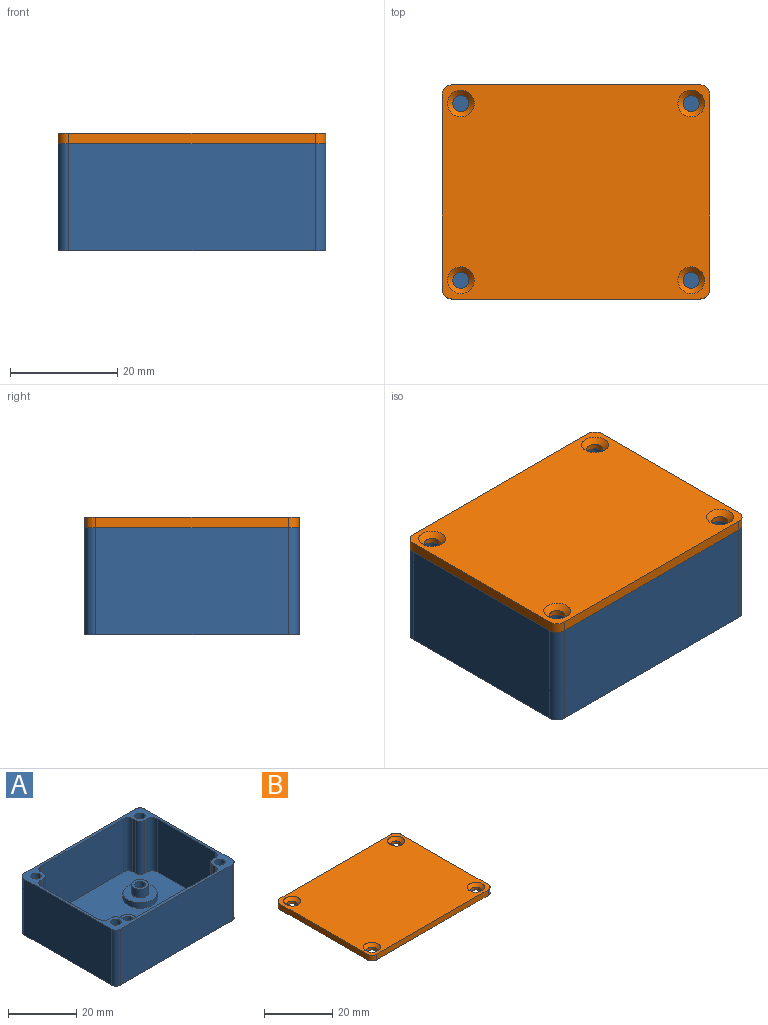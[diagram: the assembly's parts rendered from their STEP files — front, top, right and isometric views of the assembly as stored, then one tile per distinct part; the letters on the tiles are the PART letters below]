
ASSEMBLY  parts=2 mates=1
PART A: 67 faces, bbox 50x40x20 mm
  f0: cylinder r=1.5mm len=4mm, axis (0,0,-1), area 37.7mm2, adj f30,f50
  f1: cylinder r=1.5mm len=4mm, axis (0,0,-1), area 37.7mm2, adj f32,f43
  f2: plane 48x38mm, normal (0,0,1), area 1563.5mm2, adj f3,f4,f5,f6,f13,f14,f15,f16
  f3: plane 24x19mm, normal (-1,0,0), area 456mm2, adj f2,f7,f56,f57
  f4: plane 24x19mm, normal (1,0,0), area 456mm2, adj f2,f7,f53,f62
  f5: plane 34x19mm, normal (0,1,0), area 646mm2, adj f2,f7,f52,f54
  f6: plane 34x19mm, normal (0,-1,0), area 646mm2, adj f2,f7,f58,f60
  f7: plane 50x40mm, normal (0,0,1), area 247.7mm2, adj f3,f4,f5,f6,f8,f9,f10,f11
  f8: plane 46x20mm, normal (0,1,0), area 920mm2, adj f7,f12,f63,f66
  f9: plane 36x20mm, normal (-1,0,0), area 720mm2, adj f7,f12,f63,f64
  f10: plane 46x20mm, normal (0,-1,0), area 920mm2, adj f7,f12,f64,f65
  f11: plane 36x20mm, normal (1,0,0), area 720mm2, adj f7,f12,f65,f66
  f12: plane 50x40mm, normal (0,0,-1), area 1949.8mm2, adj f8,f9,f10,f11,f37,f38,f39,f40
  f13: plane 19x1mm, normal (0,-1,0), area 19mm2, adj f2,f7,f61,f62
  f14: plane 19x1mm, normal (1,0,0), area 19mm2, adj f2,f7,f60,f61
  f15: plane 19x1mm, normal (0,-1,0), area 19mm2, adj f2,f7,f57,f59
  f16: plane 19x1mm, normal (-1,0,0), area 19mm2, adj f2,f7,f58,f59
  f17: plane 19x1mm, normal (0,1,0), area 19mm2, adj f2,f7,f51,f53
  f18: plane 19x1mm, normal (1,0,0), area 19mm2, adj f2,f7,f51,f52
  f19: plane 19x1mm, normal (0,1,0), area 19mm2, adj f2,f7,f55,f56
  f20: plane 19x1mm, normal (-1,0,0), area 19mm2, adj f2,f7,f54,f55
  f21: cylinder r=1.5mm len=10mm, axis (0,0,1), area 94.2mm2, adj f7,f22
  f22: plane 3x3mm, normal (0,0,1), area 7.1mm2, adj f21
  f23: cylinder r=1.5mm len=10mm, axis (0,0,1), area 94.2mm2, adj f7,f24
  f24: plane 3x3mm, normal (0,0,1), area 7.1mm2, adj f23
  f25: cylinder r=1.5mm len=10mm, axis (0,0,1), area 94.2mm2, adj f7,f26
  f26: plane 3x3mm, normal (0,0,1), area 7.1mm2, adj f25
  f27: cylinder r=1.5mm len=10mm, axis (0,0,1), area 94.2mm2, adj f7,f28
  f28: plane 3x3mm, normal (0,0,1), area 7.1mm2, adj f27
  f29: cylinder r=2.5mm len=5mm, axis (0,0,-1), area 47.1mm2, adj f30,f36
  f30: plane 5x5mm, normal (0,0,1), area 12.6mm2, adj f0,f29
  f31: cylinder r=2.5mm len=5mm, axis (0,0,-1), area 47.1mm2, adj f32,f34
  f32: plane 5x5mm, normal (0,0,1), area 12.6mm2, adj f1,f31
  f33: cylinder r=5mm len=10mm, axis (0,0,-1), area 62.8mm2, adj f2,f34
  f34: plane 10x10mm, normal (0,0,1), area 58.9mm2, adj f31,f33
  f35: cylinder r=5mm len=10mm, axis (0,0,-1), area 62.8mm2, adj f2,f36
  f36: plane 10x10mm, normal (0,0,1), area 58.9mm2, adj f29,f35
  f37: plane 3x2mm, normal (1,0,0), area 6mm2, adj f12,f38,f42,f43
  f38: plane 2.6x2mm, normal (0.5,-0.87,0), area 6mm2, adj f12,f37,f39,f43
  f39: plane 2.6x2mm, normal (-0.5,-0.87,0), area 6mm2, adj f12,f38,f40,f43
  f40: plane 3x2mm, normal (-1,0,0), area 6mm2, adj f12,f39,f41,f43
  f41: plane 2.6x2mm, normal (-0.5,0.87,0), area 6mm2, adj f12,f40,f42,f43
  f42: plane 2.6x2mm, normal (0.5,0.87,0), area 6mm2, adj f12,f37,f41,f43
  f43: plane 6x5.2mm, normal (0,0,-1), area 16.3mm2, adj f1,f37,f38,f39,f40,f41,f42
  f44: plane 3x2mm, normal (1,0,0), area 6mm2, adj f12,f45,f49,f50
  f45: plane 2.6x2mm, normal (0.5,-0.87,0), area 6mm2, adj f12,f44,f46,f50
  f46: plane 2.6x2mm, normal (-0.5,-0.87,0), area 6mm2, adj f12,f45,f47,f50
  f47: plane 3x2mm, normal (-1,0,0), area 6mm2, adj f12,f46,f48,f50
  f48: plane 2.6x2mm, normal (-0.5,0.87,0), area 6mm2, adj f12,f47,f49,f50
  f49: plane 2.6x2mm, normal (0.5,0.87,0), area 6mm2, adj f12,f44,f48,f50
  f50: plane 6x5.2mm, normal (0,0,-1), area 16.3mm2, adj f0,f44,f45,f46,f47,f48,f49
  f51: cylinder r=2mm len=19mm, axis (0,0,1), area 59.7mm2, adj f2,f7,f17,f18
  f52: cylinder r=2mm len=19mm, axis (0,0,1), area 59.7mm2, adj f2,f5,f7,f18
  f53: cylinder r=2mm len=19mm, axis (0,0,1), area 59.7mm2, adj f2,f4,f7,f17
  f54: cylinder r=2mm len=19mm, axis (0,0,-1), area 59.7mm2, adj f2,f5,f7,f20
  f55: cylinder r=2mm len=19mm, axis (0,0,1), area 59.7mm2, adj f2,f7,f19,f20
  f56: cylinder r=2mm len=19mm, axis (0,0,1), area 59.7mm2, adj f2,f3,f7,f19
  f57: cylinder r=2mm len=19mm, axis (0,0,-1), area 59.7mm2, adj f2,f3,f7,f15
  f58: cylinder r=2mm len=19mm, axis (0,0,-1), area 59.7mm2, adj f2,f6,f7,f16
  f59: cylinder r=2mm len=19mm, axis (0,0,1), area 59.7mm2, adj f2,f7,f15,f16
  f60: cylinder r=2mm len=19mm, axis (0,0,1), area 59.7mm2, adj f2,f6,f7,f14
  f61: cylinder r=2mm len=19mm, axis (0,0,1), area 59.7mm2, adj f2,f7,f13,f14
  f62: cylinder r=2mm len=19mm, axis (0,0,-1), area 59.7mm2, adj f2,f4,f7,f13
  f63: cylinder r=2mm len=20mm, axis (0,0,1), area 62.8mm2, adj f7,f8,f9,f12
  f64: cylinder r=2mm len=20mm, axis (0,0,-1), area 62.8mm2, adj f7,f9,f10,f12
  f65: cylinder r=2mm len=20mm, axis (0,0,1), area 62.8mm2, adj f7,f10,f11,f12
  f66: cylinder r=2mm len=20mm, axis (0,0,-1), area 62.8mm2, adj f7,f8,f11,f12
PART B: 18 faces, bbox 50x40x2 mm
  f0: plane 46x2mm, normal (0,1,0), area 92mm2, adj f4,f5,f14,f17
  f1: plane 36x2mm, normal (-1,0,0), area 72mm2, adj f4,f5,f14,f15
  f2: plane 46x2mm, normal (0,-1,0), area 92mm2, adj f4,f5,f15,f16
  f3: plane 36x2mm, normal (1,0,0), area 72mm2, adj f4,f5,f16,f17
  f4: plane 50x40mm, normal (0,0,1), area 1918mm2, adj f0,f1,f2,f3,f10,f11,f12,f13
  f5: plane 50x40mm, normal (0,0,-1), area 1968.3mm2, adj f0,f1,f2,f3,f6,f7,f8,f9
  f6: cylinder r=1.5mm len=3mm, axis (0,0,1), area 9.4mm2, adj f5,f13
  f7: cylinder r=1.5mm len=3mm, axis (0,0,1), area 9.4mm2, adj f5,f12
  f8: cylinder r=1.5mm len=3mm, axis (0,0,1), area 9.4mm2, adj f5,f10
  f9: cylinder r=1.5mm len=3mm, axis (0,0,1), area 9.4mm2, adj f5,f11
  f10: cone r=1.5mm half-angle=45deg, axis (0,0,1), area 17.8mm2, adj f4,f8
  f11: cone r=1.5mm half-angle=45deg, axis (0,0,1), area 17.8mm2, adj f4,f9
  f12: cone r=1.5mm half-angle=45deg, axis (0,0,1), area 17.8mm2, adj f4,f7
  f13: cone r=1.5mm half-angle=45deg, axis (0,0,1), area 17.8mm2, adj f4,f6
  f14: cylinder r=2mm len=2mm, axis (0,0,1), area 6.3mm2, adj f0,f1,f4,f5
  f15: cylinder r=2mm len=2mm, axis (0,0,-1), area 6.3mm2, adj f1,f2,f4,f5
  f16: cylinder r=2mm len=2mm, axis (0,0,1), area 6.3mm2, adj f2,f3,f4,f5
  f17: cylinder r=2mm len=2mm, axis (0,0,-1), area 6.3mm2, adj f0,f3,f4,f5
PLACE A rot(axis=(0.14,0.97,0.21),0deg) t=(21.24,-36.65,-0.8)mm
PLACE B rot(axis=(0.14,0.97,0.21),0deg) t=(-52.22,-38.08,19.2)mm
MATE slider A.f25 <-> B.f8  axis (0,0,1) through (5.28,-15.52,19.2)mm
